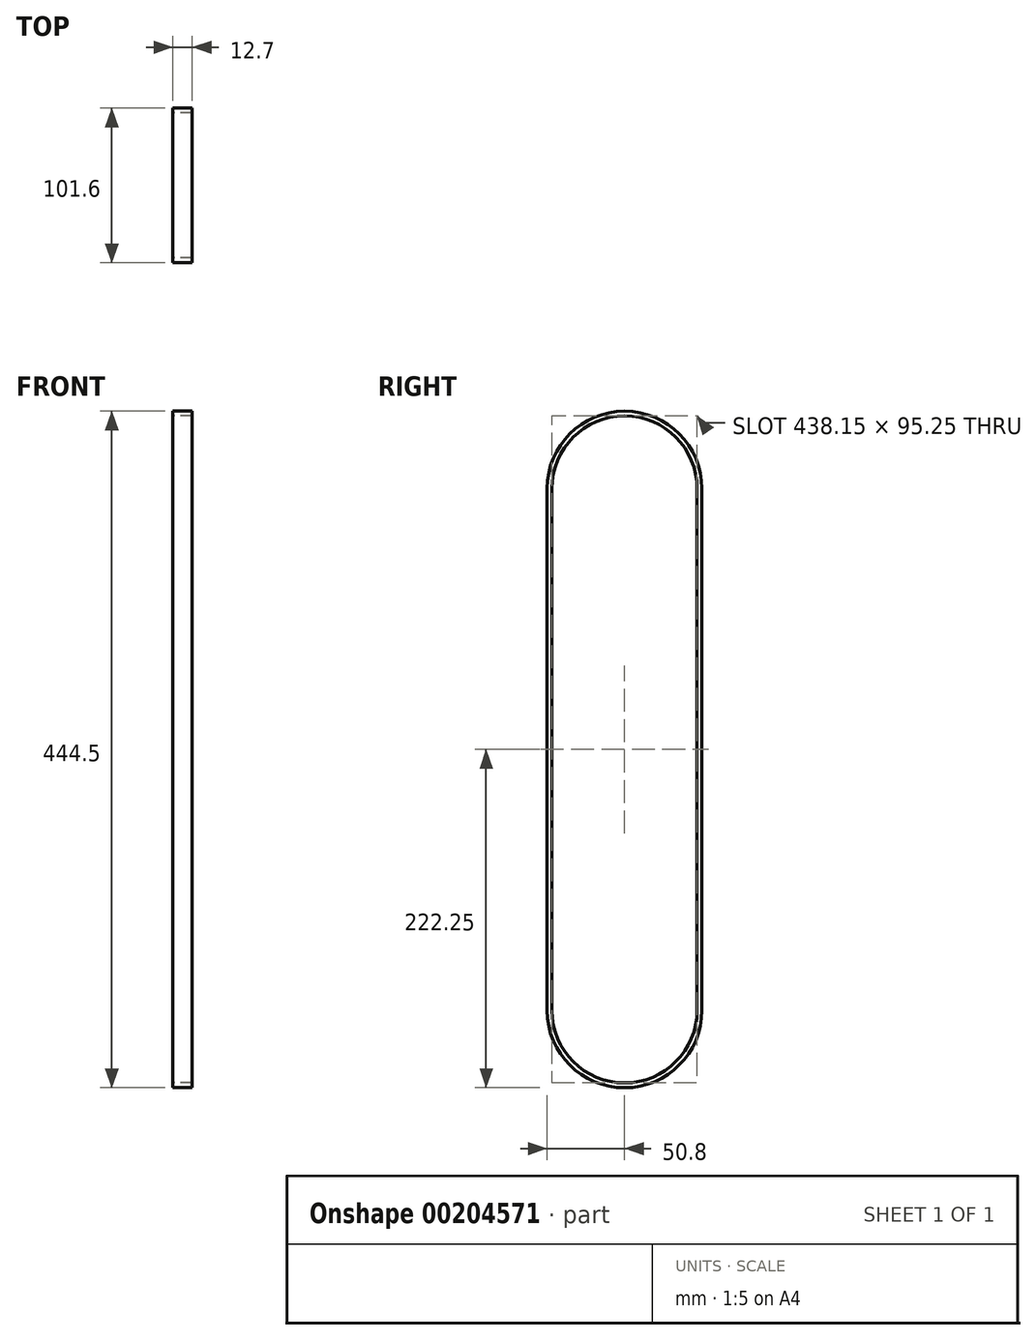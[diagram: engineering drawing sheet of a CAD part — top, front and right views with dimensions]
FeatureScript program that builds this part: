
annotation { "Feature Type Name" : "Feature", "Feature Type Description" : "" }
export const myFeature = defineFeature(function(context is Context, id is Id, definition is map)
    precondition{}
    {
        {
            var Q0;
            Q0=qCreatedBy(makeId("Right.planeOp"),FACE);
            var sketch = newSketch(context, id + "F0", { "sketchPlane" : qUnion([Q0])});
            skLineSegment(sketch, "E0", {"start": v(0, 0) * mm, "end": v(0, 342.9) * mm, "construction": true});
            skArc(sketch, "E1", {"start": v(-50.8, 0) * mm, "mid": v(0, -50.8) * mm, "end": v(50.8, 0) * mm});
            skArc(sketch, "E2", {"start": v(50.8, 342.9) * mm, "mid": v(0, 393.7) * mm, "end": v(-50.8, 342.9) * mm});
            skLineSegment(sketch, "E3", {"start": v(0, 342.9) * mm, "end": v(89.35, 342.9) * mm, "construction": true});
            skLineSegment(sketch, "E4", {"start": v(0, 0) * mm, "end": v(107.75, 0) * mm, "construction": true});
            skLineSegment(sketch, "E5", {"start": v(50.8, 342.9) * mm, "end": v(50.8, 0) * mm});
            skLineSegment(sketch, "E6.0", {"start": v(47.62, 342.9) * mm, "end": v(47.63, 0) * mm});
            skArc(sketch, "E7.0", {"start": v(47.63, 342.9) * mm, "mid": v(0, 390.53) * mm, "end": v(-47.63, 342.9) * mm});
            skArc(sketch, "E8.0", {"start": v(-47.63, 0) * mm, "mid": v(0, -47.63) * mm, "end": v(47.63, 0) * mm});
            skLineSegment(sketch, "E9.MirrorCS", {"start": v(-50.8, 342.9) * mm, "end": v(-50.8, 0) * mm});
            skLineSegment(sketch, "E10.MirrorCS", {"start": v(-47.62, 342.9) * mm, "end": v(-47.63, 0) * mm});
            skSolve(sketch);
        }
        {
            var Q0;
            Q0 = qSketchRegion(id + "F0", true);
            extrude(context, id + "F1", {"entities" : qUnion([Q0]), "endBound" : BoundingType.SYMMETRIC, "depth" : 12.7 * mm});
        }
    });
